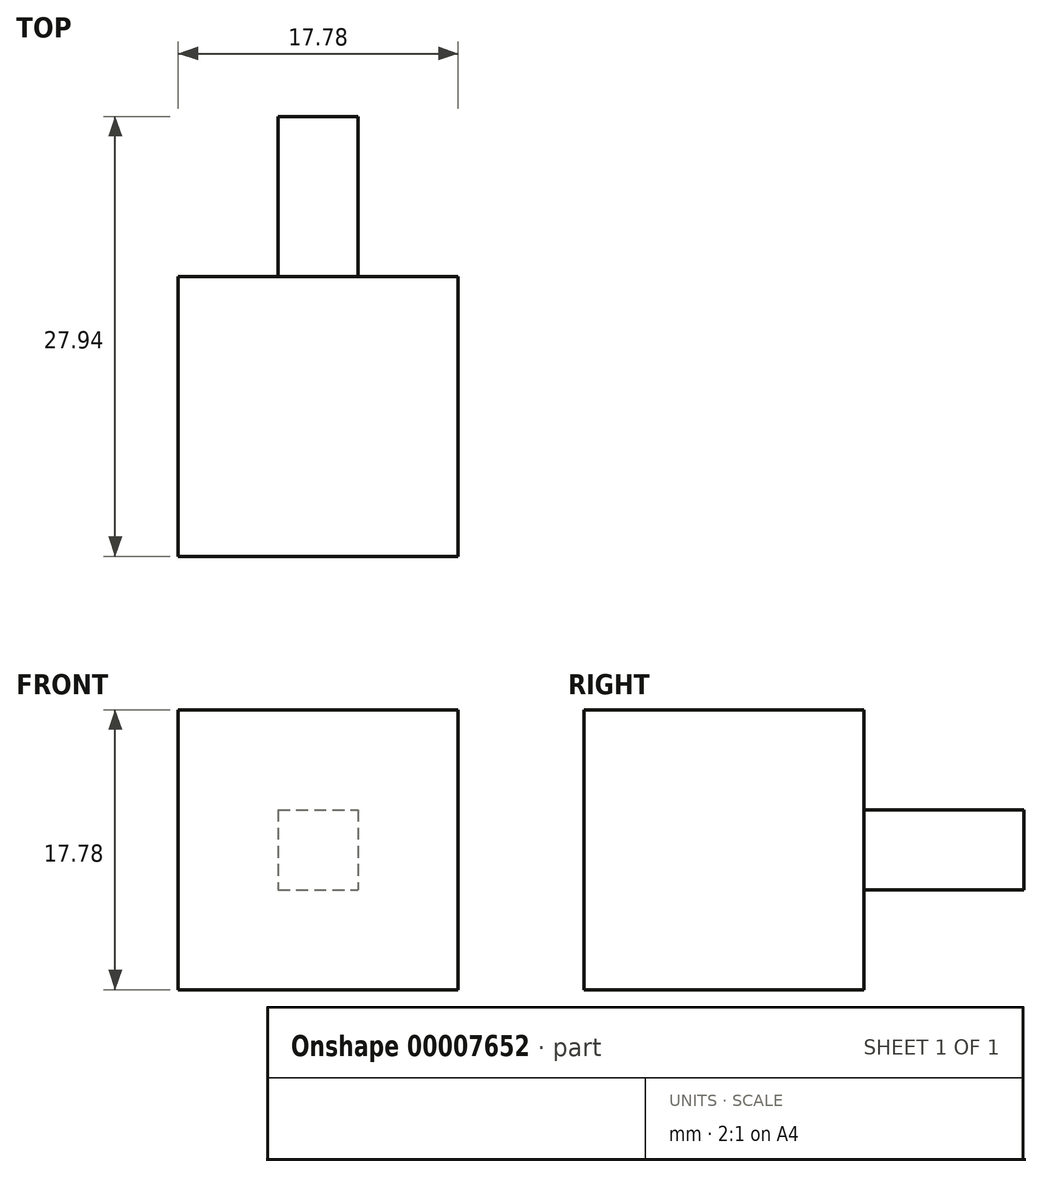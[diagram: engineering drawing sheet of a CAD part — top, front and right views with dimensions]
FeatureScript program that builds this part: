
annotation { "Feature Type Name" : "Feature", "Feature Type Description" : "" }
export const myFeature = defineFeature(function(context is Context, id is Id, definition is map)
    precondition{}
    {
        {
            var Q0;
            Q0=qCreatedBy(makeId("Front.planeOp"),FACE);
            var sketch = newSketch(context, id + "F0", { "sketchPlane" : qUnion([Q0])});
            skLineSegment(sketch, "E0.bottom", {"start": v(-2.54, 2.54) * mm, "end": v(2.54, 2.54) * mm});
            skLineSegment(sketch, "E0.top", {"start": v(-2.54, -2.54) * mm, "end": v(2.54, -2.54) * mm});
            skLineSegment(sketch, "E0.left", {"start": v(-2.54, 2.54) * mm, "end": v(-2.54, -2.54) * mm});
            skLineSegment(sketch, "E0.right", {"start": v(2.54, 2.54) * mm, "end": v(2.54, -2.54) * mm});
            skSolve(sketch);
        }
        {
            var Q0;
            Q0 = qSketchRegion(id + "F0", true);
            extrude(context, id + "F1", {"entities" : qUnion([Q0]), "depth" : 10.16 * mm});
        }
        {
            var Q0;
            Q0=makeQuery(id+"F1.opExtrude","CAP_FACE",FACE,{"disambiguationData":[OSD([sQuery(id+"F0.wireOp",EDGE,"E0.bottom"),sQuery(id+"F0.wireOp",EDGE,"E0.top"),sQuery(id+"F0.wireOp",EDGE,"E0.left"),sQuery(id+"F0.wireOp",EDGE,"E0.right")])],"isStart":false});
            var sketch = newSketch(context, id + "F2", { "sketchPlane" : qUnion([Q0])});
            skLineSegment(sketch, "E1.bottom", {"start": v(-8.89, 8.9) * mm, "end": v(8.89, 8.9) * mm});
            skLineSegment(sketch, "E1.top", {"start": v(-8.9, -8.9) * mm, "end": v(8.9, -8.9) * mm});
            skLineSegment(sketch, "E1.left", {"start": v(-8.89, 8.9) * mm, "end": v(-8.89, -8.9) * mm});
            skLineSegment(sketch, "E1.right", {"start": v(8.89, 8.9) * mm, "end": v(8.89, -8.9) * mm});
            skPoint(sketch, "E2", {"position": v(0, 2.54) * mm});
            skPoint(sketch, "E3", {"position": v(2.54, 0) * mm});
            skPoint(sketch, "E4", {"position": v(0, 0) * mm});
            skPoint(sketch, "E5", {"position": v(0, 8.9) * mm});
            skPoint(sketch, "E6", {"position": v(8.89, 0) * mm});
            skSolve(sketch);
        }
        {
            var Q0;
            Q0 = qSketchRegion(id + "F2", true);
            extrude(context, id + "F3", {"entities" : qUnion([Q0]), "operationType" : NewBodyOperationType.ADD, "depth" : 17.78 * mm});
        }
    });
